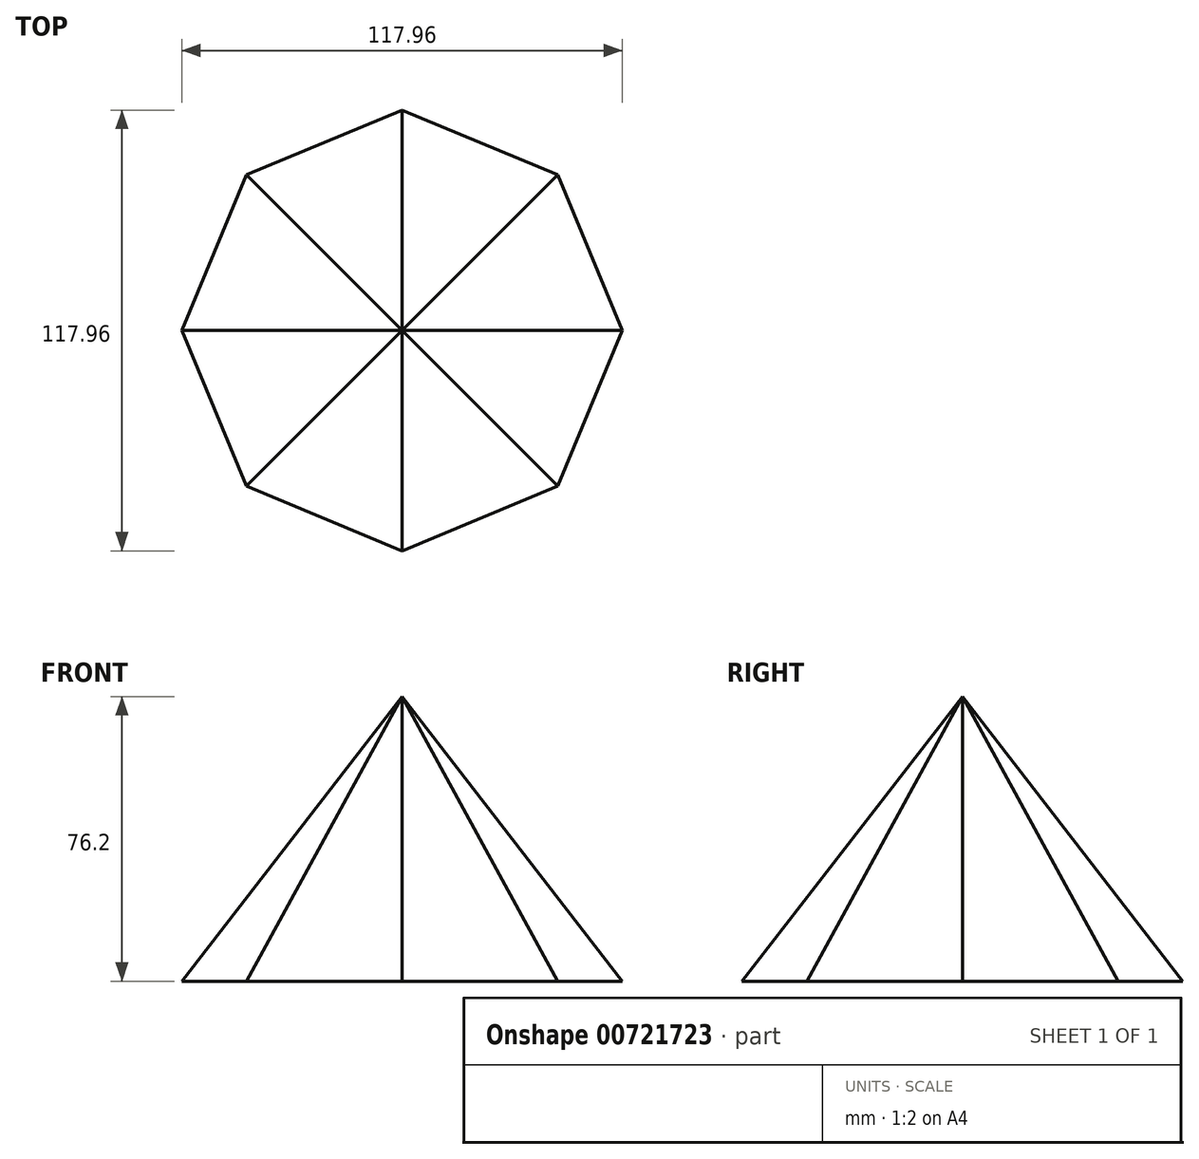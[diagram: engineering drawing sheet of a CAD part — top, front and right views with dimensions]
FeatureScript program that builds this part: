
annotation { "Feature Type Name" : "Feature", "Feature Type Description" : "" }
export const myFeature = defineFeature(function(context is Context, id is Id, definition is map)
    precondition{}
    {
        {
            var Q0;
            Q0=qCreatedBy(makeId("Top.planeOp"),FACE);
            var sketch = newSketch(context, id + "F0", { "sketchPlane" : qUnion([Q0])});
            skCircle(sketch, "E0.cCircle", {"center": v(0, 0) * mm, "radius": 54.49 * mm, "construction": true});
            skLineSegment(sketch, "E0.0", {"start": v(0, 58.98) * mm, "end": v(41.7, 41.7) * mm});
            skLineSegment(sketch, "E0.1", {"start": v(41.7, 41.7) * mm, "end": v(58.98, 0) * mm});
            skLineSegment(sketch, "E0.2", {"start": v(58.98, 0) * mm, "end": v(41.7, -41.7) * mm});
            skLineSegment(sketch, "E0.3", {"start": v(41.7, -41.7) * mm, "end": v(0, -58.98) * mm});
            skLineSegment(sketch, "E0.4", {"start": v(0, -58.98) * mm, "end": v(-41.7, -41.7) * mm});
            skLineSegment(sketch, "E0.5", {"start": v(-41.7, -41.7) * mm, "end": v(-58.98, 0) * mm});
            skLineSegment(sketch, "E0.6", {"start": v(-58.98, 0) * mm, "end": v(-41.7, 41.7) * mm});
            skLineSegment(sketch, "E0.7", {"start": v(-41.7, 41.7) * mm, "end": v(0, 58.98) * mm});
            skPoint(sketch, "E0.0.midPoint", {"position": v(20.85, 50.34) * mm});
            skSolve(sketch);
        }
        {
            var Q0;
            Q0=qCreatedBy(makeId("Top.planeOp"),FACE);
            cPlane(context, id + "F1", {"entities" : qUnion([Q0]), "cplaneType" : CPlaneType.OFFSET, "offset" : 76.2 * mm, "width" : 152.4 * mm, "height" : 152.4 * mm});
        }
        {
            var Q0;
            Q0=qCreatedBy(id+"F1.planeOp",FACE);
            var sketch = newSketch(context, id + "F2", { "sketchPlane" : qUnion([Q0])});
            skPoint(sketch, "E1", {"position": v(0, 0) * mm});
            skSolve(sketch);
        }
        {
            var Q0;
            Q0=makeQuery(id+"F0.imprint","IMPRINT",FACE,{"disambiguationData":[TD([[makeQuery(id+"F0.imprint","IMPRINT",EDGE,{"derivedFrom":sQuery(id+"F0.wireOp",EDGE,"E0.0")}),-1.0]])]});
            var Q1;
            Q1=sQuery(id+"F2.wireOp",VERTEX,"E1");
            loft(context, id + "F3", {"sheetProfilesArray" : [{ "sheetProfileEntities" : qUnion([Q0]) }, { "sheetProfileEntities" : qUnion([Q1]) }]});
        }
    });
